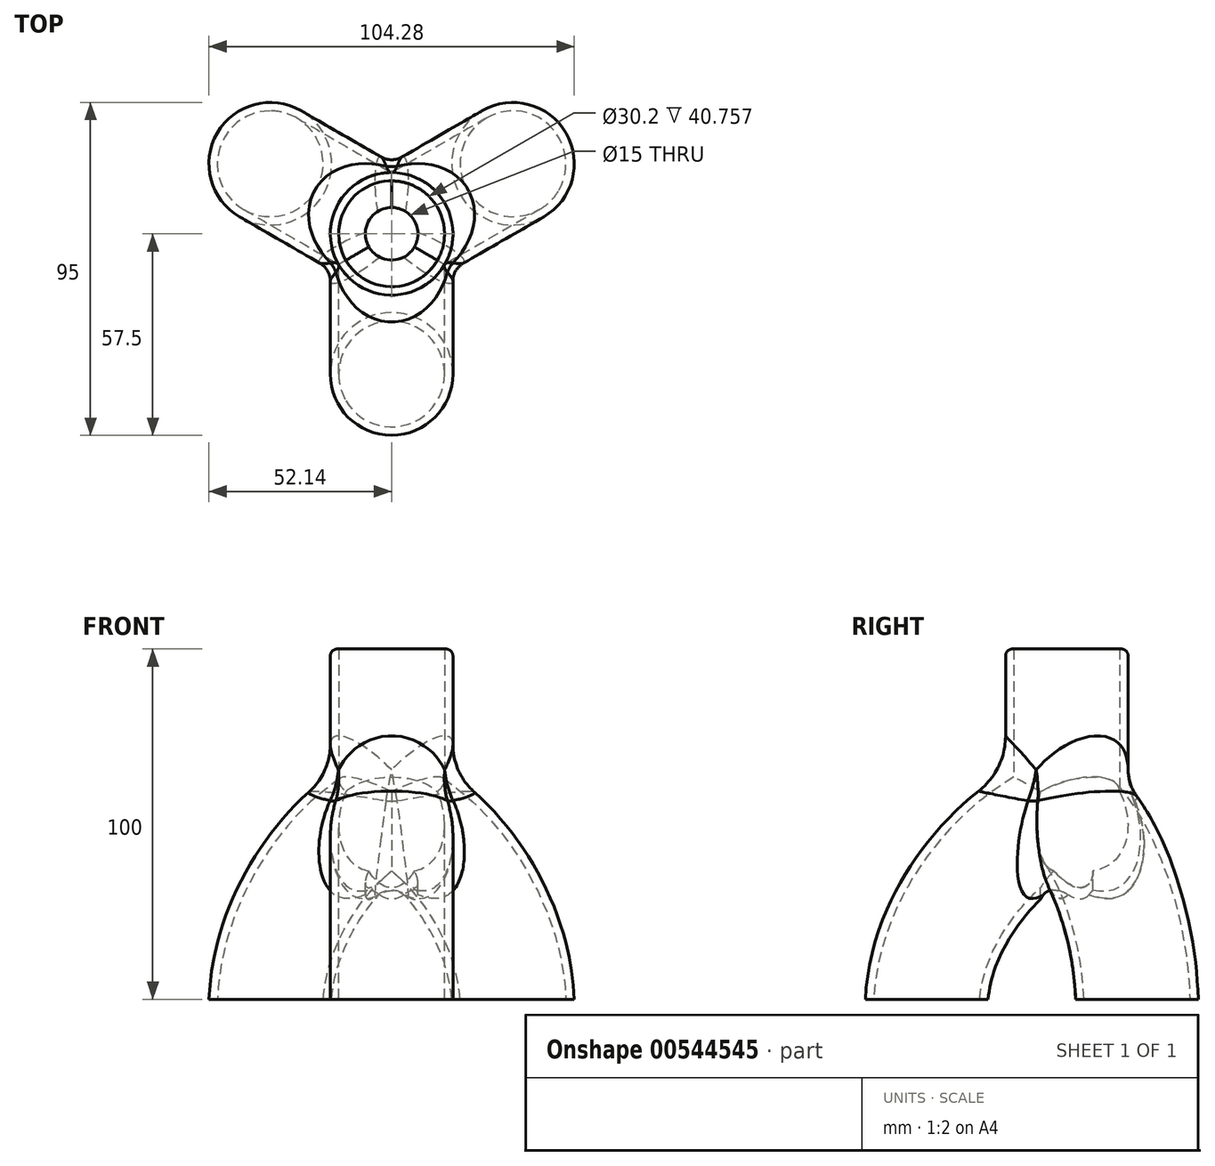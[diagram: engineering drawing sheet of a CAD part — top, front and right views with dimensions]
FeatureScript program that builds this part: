
annotation { "Feature Type Name" : "Feature", "Feature Type Description" : "" }
export const myFeature = defineFeature(function(context is Context, id is Id, definition is map)
    precondition{}
    {
        {
            var Q0;
            Q0=qCreatedBy(makeId("Top.planeOp"),FACE);
            var sketch = newSketch(context, id + "F0", { "sketchPlane" : qUnion([Q0])});
            skCircle(sketch, "E0", {"center": v(0, 0) * mm, "radius": 17.5 * mm});
            skSolve(sketch);
        }
        {
            var Q0;
            Q0 = qSketchRegion(id + "F0", true);
            extrude(context, id + "F1", {"entities" : qUnion([Q0]), "depth" : 50 * mm, "offsetDistance" : 25 * mm});
        }
        {
            var Q0;
            Q0=qCreatedBy(makeId("Right.planeOp"),FACE);
            var sketch = newSketch(context, id + "F2", { "sketchPlane" : qUnion([Q0])});
            skFitSpline(sketch, "E1", {"points": [v(0, 5) * mm, v(-20, -9.26) * mm, v(-40, -50) * mm], "startDerivative": vector(-58.51, -35.39) * mm, "endDerivative": vector(-6.07, -92.67) * mm});
            skSolve(sketch);
        }
        {
            var Q0;
            Q0=makeQuery(id+"F1.opExtrude","CAP_FACE",FACE,{"disambiguationData":[OSD([sQuery(id+"F0.wireOp",EDGE,"E0")])],"isStart":true});
            cPlane(context, id + "F3", {"entities" : qUnion([Q0]), "cplaneType" : CPlaneType.OFFSET, "offset" : 50 * mm, "width" : 150 * mm, "height" : 150 * mm});
        }
        {
            var Q0;
            Q0=qCreatedBy(id+"F3.planeOp",FACE);
            var sketch = newSketch(context, id + "F4", { "sketchPlane" : qUnion([Q0])});
            skCircle(sketch, "E2", {"center": v(0, 40) * mm, "radius": 17.5 * mm});
            skSolve(sketch);
        }
        {
            var Q0;
            Q0=makeQuery(id+"F4.imprint","IMPRINT",FACE,{"disambiguationData":[TD([[makeQuery(id+"F4.imprint","IMPRINT",EDGE,{"derivedFrom":sQuery(id+"F4.wireOp",EDGE,"E2")}),1.0]])]});
            var Q1;
            Q1=sQuery(id+"F2.wireOp",EDGE,"E1");
            sweep(context, id + "F5", {"operationType" : NewBodyOperationType.ADD, "profiles" : qUnion([Q0]), "path" : qUnion([Q1])});
        }
        {
            var Q0;
            Q0=makeQuery(id+"F1.opExtrude","SWEPT_BODY",BODY,{"disambiguationData":[OSD([sQuery(id+"F0.wireOp",EDGE,"E0")])]});
            var Q1;
            Q1=makeQuery(id+"F1.opExtrude","SWEPT_FACE",FACE,{"disambiguationData":[OSD([sQuery(id+"F0.wireOp",EDGE,"E0")])]});
            circularPattern(context, id + "F6", {"entities" : qUnion([Q0]), "axis" : qUnion([Q1]), "angle" : 360 * degree, "instanceCount" : 3, "equalSpace" : true});
        }
        {
            var Q0;
            Q0=makeQuery(id+"F6.opPattern","COPY",BODY,{"derivedFrom":makeQuery(id+"F1.opExtrude","SWEPT_BODY",BODY,{"disambiguationData":[OSD([sQuery(id+"F0.wireOp",EDGE,"E0")])]}),"instanceName":"2"});
            var Q1;
            Q1=makeQuery(id+"F6.opPattern","COPY",BODY,{"derivedFrom":makeQuery(id+"F1.opExtrude","SWEPT_BODY",BODY,{"disambiguationData":[OSD([sQuery(id+"F0.wireOp",EDGE,"E0")])]}),"instanceName":"1"});
            var Q2;
            Q2=makeQuery(id+"F1.opExtrude","SWEPT_BODY",BODY,{"disambiguationData":[OSD([sQuery(id+"F0.wireOp",EDGE,"E0")])]});
            booleanBodies(context, id + "F7", {"operationType" : BooleanOperationType.UNION, "tools" : qUnion([Q0, Q1, Q2])});
        }
        {
            var Q0;
            Q0=makeQuery(id+"F6.opPattern","COPY",FACE,{"derivedFrom":makeQuery(id+"F1.opExtrude","CAP_FACE",FACE,{"disambiguationData":[OSD([sQuery(id+"F0.wireOp",EDGE,"E0")])],"isStart":false}),"instanceName":"2"});
            var Q1;
            Q1=makeQuery(id+"F6.opPattern","COPY",FACE,{"derivedFrom":makeQuery(id+"F5.opSweep","CAP_FACE",FACE,{"disambiguationData":[OSD([sQuery(id+"F2.wireOp",VERTEX,"E1.end"),sQuery(id+"F4.wireOp",EDGE,"E2")])],"isStart":true}),"instanceName":"1"});
            var Q2;
            Q2=makeQuery(id+"F5.opSweep","CAP_FACE",FACE,{"disambiguationData":[OSD([sQuery(id+"F2.wireOp",VERTEX,"E1.end"),sQuery(id+"F4.wireOp",EDGE,"E2")])],"isStart":true});
            var Q3;
            Q3=makeQuery(id+"F6.opPattern","COPY",FACE,{"derivedFrom":makeQuery(id+"F5.opSweep","CAP_FACE",FACE,{"disambiguationData":[OSD([sQuery(id+"F2.wireOp",VERTEX,"E1.end"),sQuery(id+"F4.wireOp",EDGE,"E2")])],"isStart":true}),"instanceName":"2"});
            shell(context, id + "F8", {"entities" : qUnion([Q0, Q1, Q2, Q3]), "thickness" : 2.4 * mm});
        }
        {
            var Q0;
            Q0=makeQuery(id+"F6.opPattern","COPY",EDGE,{"derivedFrom":makeQuery(id+"F1.opExtrude","CAP_EDGE",EDGE,{"disambiguationData":[OSD([sQuery(id+"F0.wireOp",EDGE,"E0")])],"isStart":false}),"instanceName":"2"});
            fillet(context, id + "F9", {"entities" : qUnion([Q0]), "radius" : 2 * mm, "tangentPropagation" : true, "allowEdgeOverflow" : false});
        }
        {
            var Q0;
            Q0=qCreatedBy(makeId("Top.planeOp"),FACE);
            var sketch = newSketch(context, id + "F10", { "sketchPlane" : qUnion([Q0])});
            skCircle(sketch, "E3", {"center": v(0, 0) * mm, "radius": 7.5 * mm});
            skSolve(sketch);
        }
        {
            var Q0;
            Q0=makeQuery(id+"F10.imprint","IMPRINT",FACE,{"disambiguationData":[TD([[makeQuery(id+"F10.imprint","IMPRINT",EDGE,{"derivedFrom":sQuery(id+"F10.wireOp",EDGE,"E3")}),1.0]])]});
            extrude(context, id + "F11", {"entities" : qUnion([Q0]), "operationType" : NewBodyOperationType.REMOVE, "oppositeDirection" : true, "depth" : 25 * mm, "offsetDistance" : 25 * mm});
        }
        {
            var Q0;
            {var subQ0=makeQuery(id+"F5.opSweep","SWEPT_FACE",FACE,{"disambiguationData":[OSD([sQuery(id+"F2.wireOp",EDGE,"E1"),sQuery(id+"F4.wireOp",EDGE,"E2")])]});Q0=makeQuery(id+"F7.opBoolean","INTERSECT",EDGE,{"derivedFrom":[makeQuery(id+"F6.opPattern","COPY",FACE,{"derivedFrom":subQ0,"instanceName":"1"}),makeQuery(id+"F6.opPattern","COPY",FACE,{"derivedFrom":subQ0,"instanceName":"2"})]});}
            fillet(context, id + "F12", {"entities" : qUnion([Q0]), "radius" : 6 * mm, "tangentPropagation" : true, "allowEdgeOverflow" : false});
        }
        {
            var Q0;
            Q0=makeQuery(id+"F6.opPattern","COPY",EDGE,{"derivedFrom":makeQuery(id+"F5.boolean.opBoolean","INTERSECT",EDGE,{"disambiguationData":[OD(0.0)],"derivedFrom":[makeQuery(id+"F1.opExtrude","SWEPT_FACE",FACE,{"disambiguationData":[OSD([sQuery(id+"F0.wireOp",EDGE,"E0")])]}),makeQuery(id+"F5.opSweep","SWEPT_FACE",FACE,{"disambiguationData":[OSD([sQuery(id+"F2.wireOp",EDGE,"E1"),sQuery(id+"F4.wireOp",EDGE,"E2")])]})]}),"instanceName":"2"});
            fillet(context, id + "F13", {"entities" : qUnion([Q0]), "radius" : 20 * mm, "tangentPropagation" : true, "allowEdgeOverflow" : false});
        }
        {
            var Q0;
            {var subQ0=makeQuery(id+"F1.opExtrude","SWEPT_FACE",FACE,{"disambiguationData":[OSD([sQuery(id+"F0.wireOp",EDGE,"E0")])]});Q0=makeQuery(id+"F7.opBoolean","INTERSECT",EDGE,{"derivedFrom":[makeQuery(id+"F6.opPattern","COPY",FACE,{"derivedFrom":subQ0,"instanceName":"1"}),makeQuery(id+"F6.opPattern","COPY",FACE,{"derivedFrom":subQ0,"instanceName":"2"})]});}
            fillet(context, id + "F14", {"entities" : qUnion([Q0]), "radius" : 20 * mm, "tangentPropagation" : true, "allowEdgeOverflow" : false});
        }
        {
            var Q0;
            {var subQ0=makeQuery(id+"F5.opSweep","SWEPT_FACE",FACE,{"disambiguationData":[OSD([sQuery(id+"F2.wireOp",EDGE,"E1"),sQuery(id+"F4.wireOp",EDGE,"E2")])]});Q0=makeQuery(id+"F7.opBoolean","INTERSECT",EDGE,{"derivedFrom":[subQ0,makeQuery(id+"F6.opPattern","COPY",FACE,{"derivedFrom":subQ0,"instanceName":"1"})]});}
            fillet(context, id + "F15", {"entities" : qUnion([Q0]), "radius" : 6 * mm, "tangentPropagation" : true, "allowEdgeOverflow" : false});
        }
        {
            var Q0;
            {var subQ0=makeQuery(id+"F5.opSweep","SWEPT_FACE",FACE,{"disambiguationData":[OSD([sQuery(id+"F2.wireOp",EDGE,"E1"),sQuery(id+"F4.wireOp",EDGE,"E2")])]});Q0=makeQuery(id+"F7.opBoolean","INTERSECT",EDGE,{"derivedFrom":[subQ0,makeQuery(id+"F6.opPattern","COPY",FACE,{"derivedFrom":subQ0,"instanceName":"2"})]});}
            fillet(context, id + "F16", {"entities" : qUnion([Q0]), "radius" : 6 * mm, "tangentPropagation" : true, "allowEdgeOverflow" : false});
        }
    });
